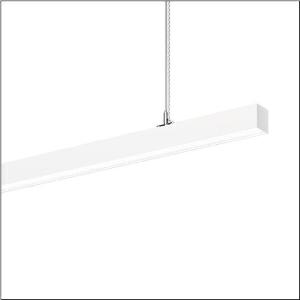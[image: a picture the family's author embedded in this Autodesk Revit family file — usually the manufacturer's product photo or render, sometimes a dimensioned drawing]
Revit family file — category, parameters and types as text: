
# Revit family: silica_r__21_51mx33dc3dwb_1062
name_source: partatom
category: Lighting Fixtures
units: mm (PartAtom-declared; Revit-internal decimal feet)

## family parameters
Cut with Voids When Loaded = No
Host = Face
Light Source = No
Part Type = Normal
Room Calculation Point = No
Round Connector Dimension = Use Diameter
Shared = No

## types (1)
- --- (1 x LED, 14780 lm, 99.5 W, 3000K)
    Apparent Load = 100 VA
    CIE Flux Codes = 78 96 99 55 100
    Color Rendering = 80
    Color Temperature = 3000K
    Default Elevation = 1800 mm
    Description = Silica® 21, office luminaire, primary optical cover: prismatic diffuser, of PMMA, CAT 2 (L<= 3000cd/m²), light emission: direct/indirect distribution, primary light characteristic: symmetric, installation type: suspended mounting, LED, rated luminous flux: 14.780lm, luminous efficacy: 149lm/W, light colour: 830, colour temperature: 3000K, with terminal, 3+2-pole, max. 2.5mm², mains connection: 220..240V, AC, 50/60Hz, rated input power: 99.5W, luminaire housing, of aluminium, traffic white (RAL 9016), length: 3.004mm, width: 53mm, height: 53mm, protection rating (complete): IP20, insulation class (complete): insulation class I (protective earthing), certification: CE, permissible operating ambient temperature: 0..+35°C, standard: EN 50419, packaging unit: 1 piece
    Height = 53 mm
    Lamp = 1 x LED
    Lamp Light Flux = 14780 lm
    Lamp Power = 99.5 W
    Lamp count = 1
    Length = 3004 mm
    Luminous efficacy = 149 lm/W
    Manufacturer = Siteco
    ModVariant = No
    Model = 51MX33DC3DWB
    Mounting Place = Ceiling
    Mounting Type = Pendant
    Number of Poles = 1
    OnlyDefault = Yes
    Power Factor = 1
    Product Name = Silica® 21
    Product group = office luminaire | ceiling pendant
    ProductGroupID = 902
    Protection Class = Protection class I
    Protection Degree = IP 20
    RLX_Detail_Level = 1
    RLX_Emergency_Light_Flux = 0 lm
    RLX_Emergency_Type = 0
    RLX_Emergency_Type_DB = No
    RlxData = <blob elided: 21441 chars, md5=32636811>
    Socket = socket
    Standby Power = 0 W
    System Light Flux = 14780 lm
    System Power = 100 W
    Type Comments = factory setting: luminous flux: 100 % | dim-lin: 254 | 345 mA
    Type Image = l_1313629.jpg
    URL = http://relux.com
    VarID = @adj_067311
    Voltage = 0 V
    Weight = 0.00 kg
    Width = 53 mm

## geometry (parser evidence)
native form markers: Blend x4, Sweep x12
no freeform markers — native parametric forms only
